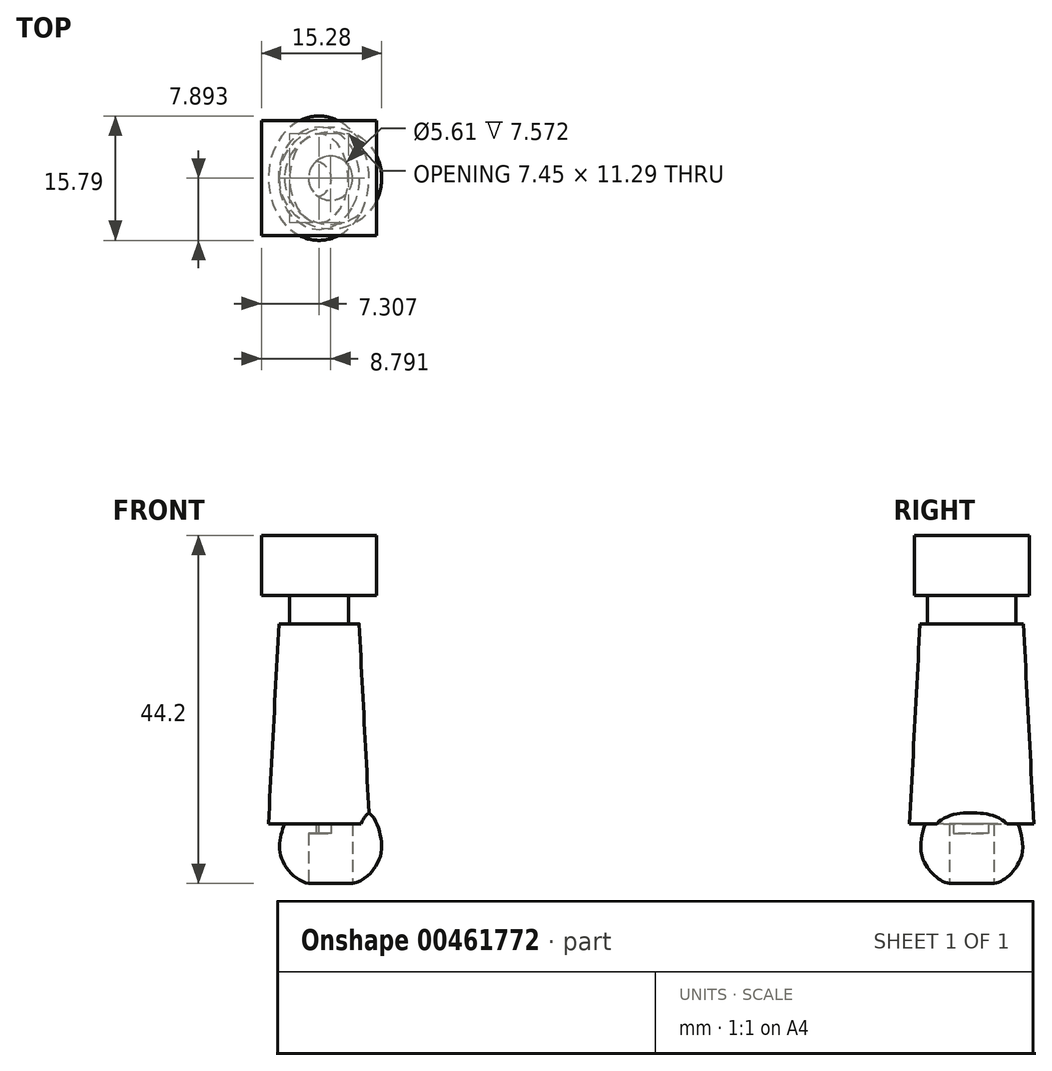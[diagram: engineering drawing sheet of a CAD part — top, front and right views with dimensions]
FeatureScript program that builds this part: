
annotation { "Feature Type Name" : "Feature", "Feature Type Description" : "" }
export const myFeature = defineFeature(function(context is Context, id is Id, definition is map)
    precondition{}
    {
        {
            var Q0;
            Q0=qCreatedBy(makeId("Top.planeOp"),FACE);
            var sketch = newSketch(context, id + "F0", { "sketchPlane" : qUnion([Q0])});
            skLineSegment(sketch, "E0", {"start": v(0, 0) * mm, "end": v(0, 14.6) * mm});
            skLineSegment(sketch, "E1", {"start": v(0, 14.6) * mm, "end": v(-14.6, 14.6) * mm});
            skLineSegment(sketch, "E2", {"start": v(-14.6, 14.6) * mm, "end": v(-14.6, 0) * mm});
            skLineSegment(sketch, "E3", {"start": v(-14.6, 0) * mm, "end": v(0, 0) * mm});
            skSolve(sketch);
        }
        {
            var Q0;
            Q0=makeQuery(id+"F0.imprint","IMPRINT",FACE,{"disambiguationData":[TD([[makeQuery(id+"F0.imprint","IMPRINT",EDGE,{"derivedFrom":sQuery(id+"F0.wireOp",EDGE,"E0")}),1.0]])]});
            extrude(context, id + "F1", {"entities" : qUnion([Q0]), "depth" : 7.62 * mm});
        }
        {
            var Q0;
            Q0=qCreatedBy(makeId("Top.planeOp"),FACE);
            var sketch = newSketch(context, id + "F2", { "sketchPlane" : qUnion([Q0])});
            skLineSegment(sketch, "E4", {"start": v(0, 0) * mm, "end": v(-7.3, 0) * mm});
            skLineSegment(sketch, "E5", {"start": v(-7.3, 0) * mm, "end": v(-7.3, 7.3) * mm});
            skEllipse(sketch, "E6", {"center": v(-7.3, 7.3) * mm, "majorRadius": 5.65 * mm, "minorRadius": 3.72 * mm, "majorAxis": v(0, -1)});
            skSolve(sketch);
        }
        {
            var Q0;
            Q0=makeQuery(id+"F2.imprint","IMPRINT",FACE,{"disambiguationData":[TD([[makeQuery(id+"F2.imprint","IMPRINT",EDGE,{"derivedFrom":sQuery(id+"F2.wireOp",EDGE,"E6")}),1.0]])]});
            extrude(context, id + "F3", {"entities" : qUnion([Q0]), "operationType" : NewBodyOperationType.ADD, "oppositeDirection" : true, "depth" : 3.6 * mm});
        }
        {
            var Q0;
            Q0=makeQuery(id+"F3.opExtrude","CAP_FACE",FACE,{"disambiguationData":[OSD([sQuery(id+"F2.wireOp",EDGE,"E6")])],"isStart":false});
            var sketch = newSketch(context, id + "F4", { "sketchPlane" : qUnion([Q0])});
            skEllipse(sketch, "E7", {"center": v(-7.3, -7.3) * mm, "majorRadius": 6.56 * mm, "minorRadius": 5.1 * mm, "majorAxis": v(0, 1)});
            skSolve(sketch);
        }
        {
            var Q0;
            Q0=makeQuery(id+"F4.imprint","IMPRINT",FACE,{"disambiguationData":[TD([[makeQuery(id+"F4.imprint","IMPRINT",EDGE,{"derivedFrom":sQuery(id+"F4.wireOp",EDGE,"E7")}),1.0]])]});
            var Q1;
            Q1=makeQuery(id+"F4.imprint","IMPRINT",FACE,{"disambiguationData":[TD([[makeQuery(id+"F4.imprint","IMPRINT",EDGE,{"derivedFrom":makeQuery(id+"F3.opExtrude","CAP_EDGE",EDGE,{"disambiguationData":[OSD([sQuery(id+"F2.wireOp",EDGE,"E6")])],"isStart":false})}),-1.0]])]});
            extrude(context, id + "F5", {"entities" : qUnion([Q0, Q1]), "operationType" : NewBodyOperationType.ADD, "depth" : 25.4 * mm, "hasDraft" : true, "draftAngle" : 3 * degree});
        }
        {
            var Q0;
            Q0=makeQuery(id+"F5.opExtrude","CAP_FACE",FACE,{"disambiguationData":[OSD([sQuery(id+"F4.wireOp",EDGE,"E7")])],"isStart":false});
            var sketch = newSketch(context, id + "F6", { "sketchPlane" : qUnion([Q0])});
            skCircle(sketch, "E8", {"center": v(-8.02, -7.17) * mm, "radius": 2.29 * mm});
            skSolve(sketch);
        }
        {
            var Q0;
            Q0=makeQuery(id+"F6.imprint","IMPRINT",FACE,{"disambiguationData":[TD([[makeQuery(id+"F6.imprint","IMPRINT",EDGE,{"derivedFrom":sQuery(id+"F6.wireOp",EDGE,"E8")}),1.0]])]});
            extrude(context, id + "F7", {"entities" : qUnion([Q0]), "operationType" : NewBodyOperationType.ADD, "depth" : 1.22 * mm});
        }
        {
            var Q0;
            Q0=makeQuery(id+"F1.opExtrude","SWEPT_FACE",FACE,{"disambiguationData":[OSD([sQuery(id+"F0.wireOp",EDGE,"E1")])]});
            var Q1;
            Q1=makeQuery(id+"F1.opExtrude","SWEPT_FACE",FACE,{"disambiguationData":[OSD([sQuery(id+"F0.wireOp",EDGE,"E3")])]});
            cPlane(context, id + "F8", {"entities" : qUnion([Q0, Q1]), "cplaneType" : CPlaneType.MID_PLANE, "offset" : 25.4 * mm, "width" : 152.4 * mm, "height" : 152.4 * mm});
        }
        {
            var Q0;
            Q0=qCreatedBy(id+"F8.planeOp",FACE);
            var sketch = newSketch(context, id + "F9", { "sketchPlane" : qUnion([Q0])});
            skLineSegment(sketch, "E9", {"start": v(5.82, -36.58) * mm, "end": v(5.82, -16.52) * mm});
            skLineSegment(sketch, "E10", {"start": v(8.63, -36.58) * mm, "end": v(8.63, -27.04) * mm});
            skFitSpline(sketch, "E11", {"points": [v(8.63, -36.58) * mm, v(12.03, -33.42) * mm, v(11.95, -29.78) * mm, v(10.7, -27.62) * mm, v(8.63, -27.04) * mm], "startDerivative": vector(14.29, 2.19) * mm, "endDerivative": vector(-9.6, 1.58) * mm});
            skSolve(sketch);
        }
        {
            var Q0;
            Q0=makeQuery(id+"F9.imprint","IMPRINT",FACE,{"disambiguationData":[TD([[makeQuery(id+"F9.imprint","IMPRINT",EDGE,{"derivedFrom":sQuery(id+"F9.wireOp",EDGE,"E10")}),-1.0]])]});
            var Q1;
            Q1=sQuery(id+"F9.wireOp",EDGE,"E9");
            revolve(context, id + "F10", {"operationType" : NewBodyOperationType.ADD, "entities" : qUnion([Q0]), "axis" : qUnion([Q1]), "revolveType" : RevolveType.FULL});
        }
    });
